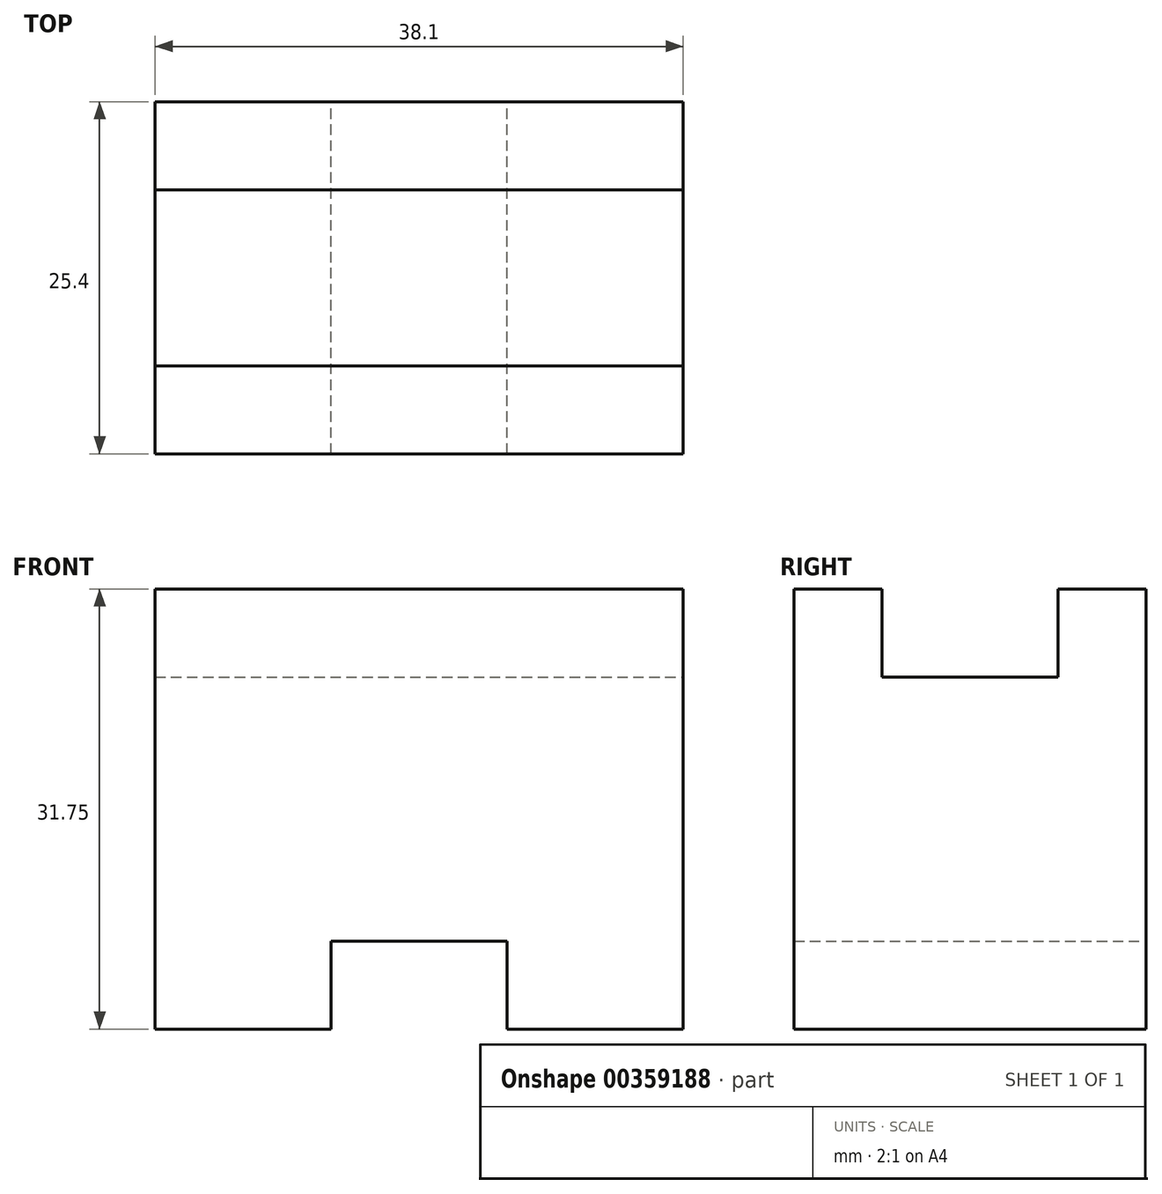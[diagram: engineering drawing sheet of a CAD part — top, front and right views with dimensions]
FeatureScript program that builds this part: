
annotation { "Feature Type Name" : "Feature", "Feature Type Description" : "" }
export const myFeature = defineFeature(function(context is Context, id is Id, definition is map)
    precondition{}
    {
        {
            var Q0;
            Q0=qCreatedBy(makeId("Front.planeOp"),FACE);
            var sketch = newSketch(context, id + "F0", { "sketchPlane" : qUnion([Q0])});
            skLineSegment(sketch, "E0", {"start": v(0, 0) * mm, "end": v(0, 31.75) * mm});
            skLineSegment(sketch, "E1", {"start": v(0, 31.75) * mm, "end": v(38.1, 31.75) * mm});
            skLineSegment(sketch, "E2", {"start": v(38.1, 31.75) * mm, "end": v(38.1, 0) * mm});
            skLineSegment(sketch, "E3", {"start": v(0, 0) * mm, "end": v(38.1, 0) * mm});
            skLineSegment(sketch, "E4", {"start": v(12.7, 0) * mm, "end": v(12.7, 6.35) * mm});
            skLineSegment(sketch, "E5", {"start": v(12.7, 6.35) * mm, "end": v(25.4, 6.35) * mm});
            skLineSegment(sketch, "E6", {"start": v(25.4, 6.35) * mm, "end": v(25.4, 0) * mm});
            skLineSegment(sketch, "E7", {"start": v(12.7, 0) * mm, "end": v(25.4, 0) * mm});
            skSolve(sketch);
        }
        {
            var Q0;
            {var subQ1=sQuery(id+"F0.wireOp",EDGE,"E0");Q0=makeQuery(id+"F0.imprint","IMPRINT",FACE,{"disambiguationData":[TD([[makeQuery(id+"F0.imprint","IMPRINT",EDGE,{"derivedFrom":subQ1}),-1.0]])]});}
            extrude(context, id + "F1", {"entities" : qUnion([Q0]), "depth" : 25.4 * mm});
        }
        {
            var Q0;
            Q0=makeQuery(id+"F1.opExtrude","SWEPT_FACE",FACE,{"disambiguationData":[OSD([sQuery(id+"F0.wireOp",EDGE,"E2")])]});
            var sketch = newSketch(context, id + "F2", { "sketchPlane" : qUnion([Q0])});
            skLineSegment(sketch, "E8", {"start": v(-19.05, 31.75) * mm, "end": v(-19.05, 25.4) * mm});
            skLineSegment(sketch, "E9", {"start": v(-19.05, 25.4) * mm, "end": v(-6.35, 25.4) * mm});
            skLineSegment(sketch, "E10", {"start": v(-6.35, 25.4) * mm, "end": v(-6.35, 31.75) * mm});
            skSolve(sketch);
        }
        {
            var Q0;
            Q0 = qSketchRegion(id + "F2", true);
            var Q1;
            {var subQ0=sQuery(id+"F2.wireOp",EDGE,"E8");Q1=makeQuery(id+"F2.imprint","IMPRINT",FACE,{"disambiguationData":[TD([[makeQuery(id+"F2.imprint","IMPRINT",EDGE,{"derivedFrom":subQ0}),1.0]])]});}
            extrude(context, id + "F3", {"entities" : qUnion([Q0, Q1]), "operationType" : NewBodyOperationType.REMOVE, "oppositeDirection" : true, "depth" : 25.4 * mm});
        }
        {
            var Q0;
            Q0=makeQuery(id+"F3.boolean.opBoolean","COPY",FACE,{"derivedFrom":makeQuery(id+"F3.opExtrude","CAP_FACE",FACE,{"disambiguationData":[OSD([sQuery(id+"F0.wireOp",EDGE,"E1"),sQuery(id+"F0.wireOp",EDGE,"E2"),sQuery(id+"F2.wireOp",EDGE,"E8"),sQuery(id+"F2.wireOp",EDGE,"E9"),sQuery(id+"F2.wireOp",EDGE,"E10")])],"isStart":false})});
            extrude(context, id + "F4", {"entities" : qUnion([Q0]), "operationType" : NewBodyOperationType.REMOVE, "oppositeDirection" : true, "depth" : 25.4 * mm});
        }
    });
